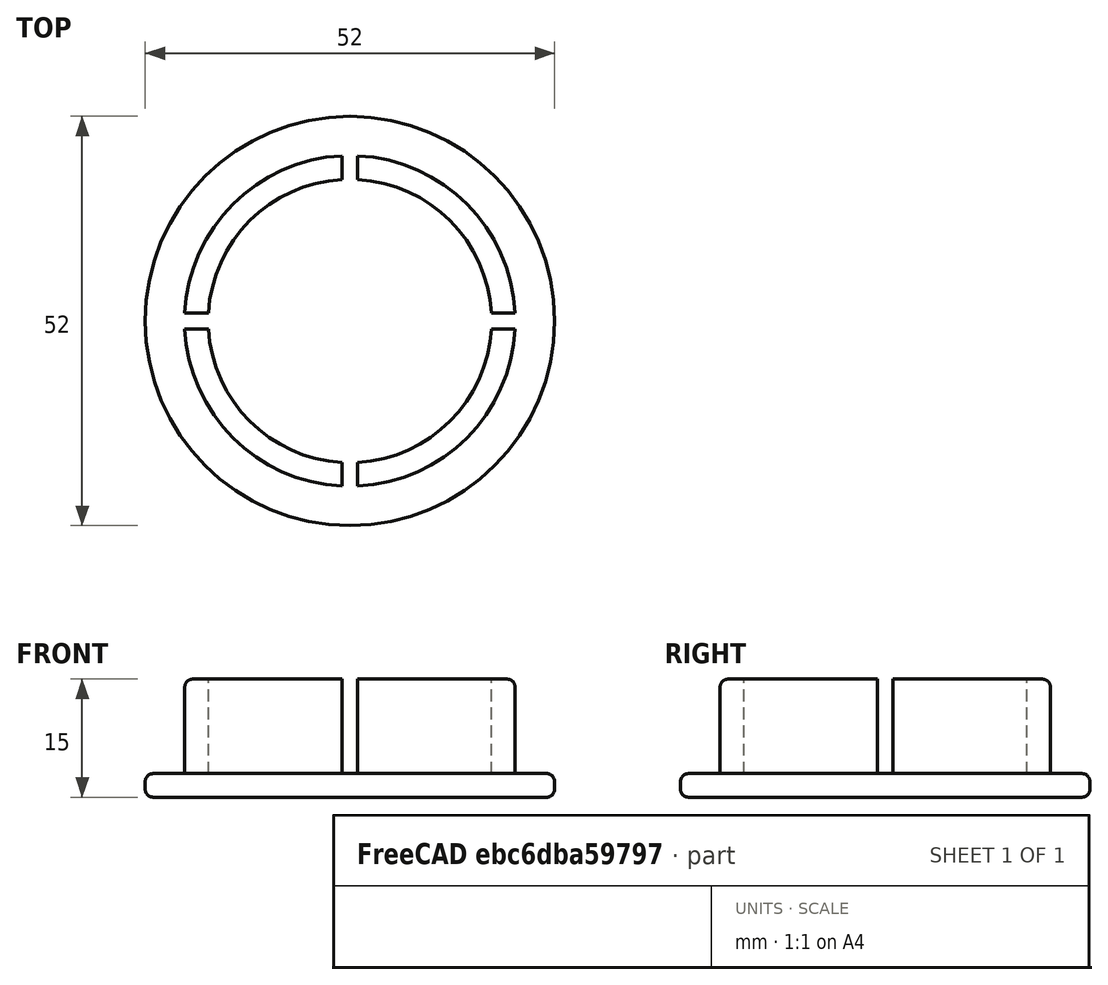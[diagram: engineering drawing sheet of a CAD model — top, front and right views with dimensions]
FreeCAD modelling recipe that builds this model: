
FCSTD DOCUMENT  (FreeCAD 0.18R4 (GitTag))
Label: OnStep for GS80cap
License: All rights reserved
LicenseURL: http://en.wikipedia.org/wiki/All_rights_reserved
objects: Part::Cylinder×3, Part::Box×2, Part::MultiFuse×2, Part::Cut×1, Part::Fillet×1, Part::Feature×1
note: 10 computed .brp shape members not serialized (recipe doc carries the construction recipe); baked Part::Feature solids carry a one-line shape summary decoded from their .brp

FEATURE [Part::Cylinder] Cylinder  label="Válec"
  Angle = 360
  AttacherType = Attacher::AttachEngine3D
  Height = 15
  Radius = 21
FEATURE [Part::Cylinder] Cylinder001  label="Válec001"
  Angle = 360
  AttacherType = Attacher::AttachEngine3D
  Height = 3
  Radius = 26
FEATURE [Part::Cylinder] Cylinder002  label="Válec002"
  Angle = 360
  AttacherType = Attacher::AttachEngine3D
  Height = 12
  Placement = pos=(0,0,3) rot=(0,0,1;0rad)
  Radius = 18
FEATURE [Part::Box] Box  label="Krychle"
  AttacherType = Attacher::AttachEngine3D
  Height = 12
  Length = 42
  Placement = pos=(-21,-1,3) rot=(0,0,1;0rad)
  Width = 2
FEATURE [Part::Box] Box001  label="Krychle001"
  AttacherType = Attacher::AttachEngine3D
  Height = 12
  Length = 2
  Placement = pos=(-1,-21,3) rot=(0,0,1;0rad)
  Width = 42
FEATURE [Part::MultiFuse] Fusion
  Shapes = -> [Cylinder002,Box,Box001]
FEATURE [Part::MultiFuse] Fusion001
  Shapes = -> [Cylinder,Cylinder001]
FEATURE [Part::Cut] Cut
  Base = -> Fusion001
  Tool = -> Fusion
FEATURE [Part::Fillet] Fillet
  Base = -> Cut
  Edges = 6 edges r=1: [Edge4,Edge29,Edge31,Edge36,Edge41,Edge46]
FEATURE [Part::Feature] Fillet001
  shape: bbox 56.29 x 56.29 x 15 mm, 29 faces (baked)
